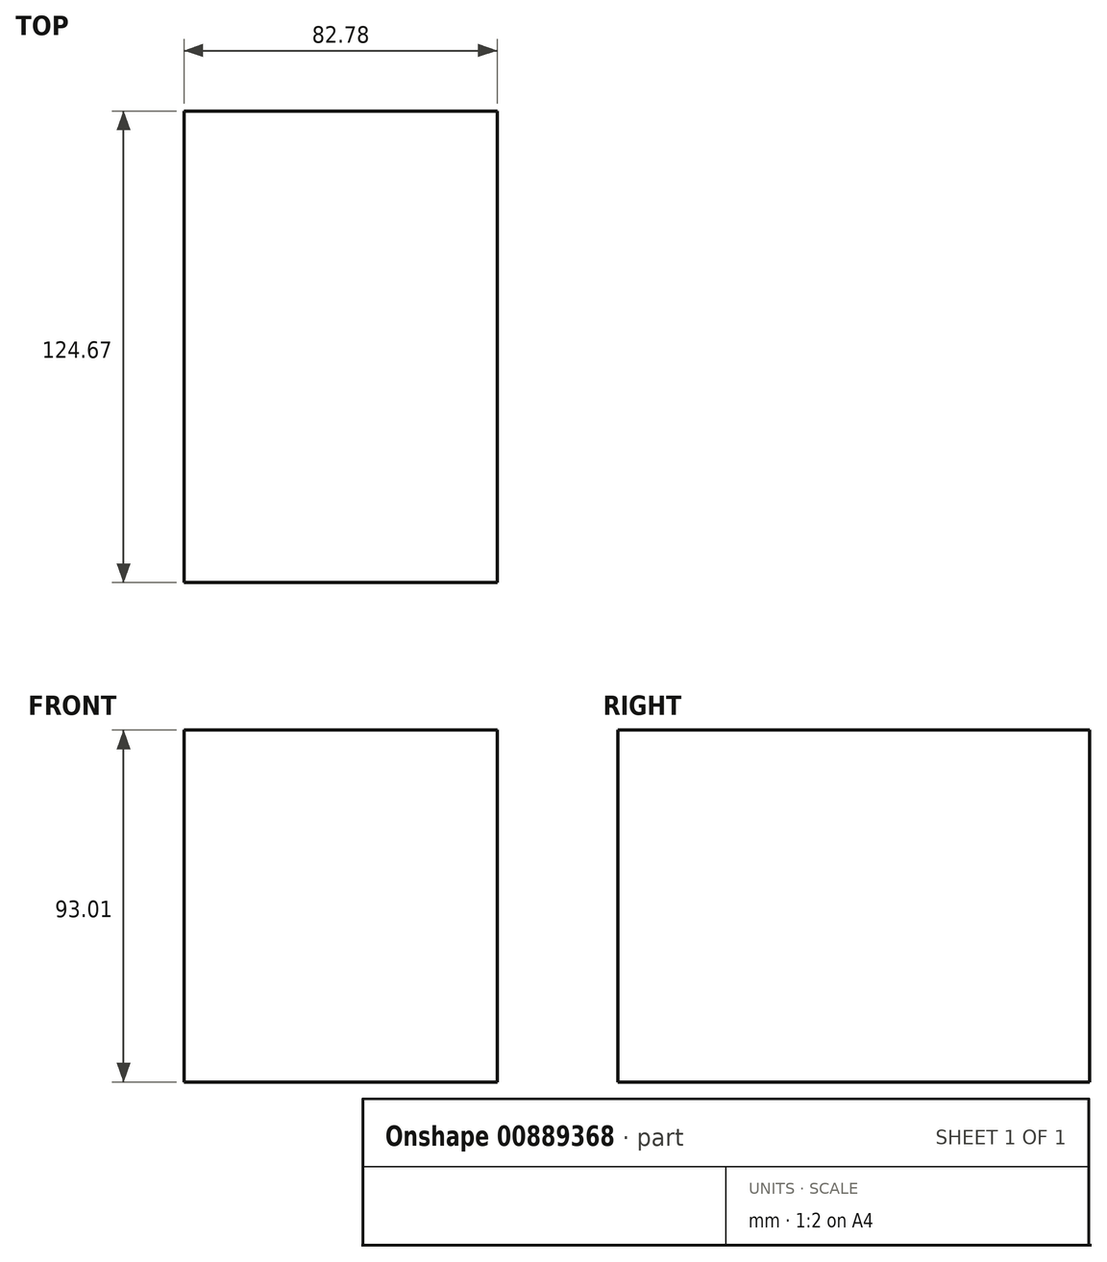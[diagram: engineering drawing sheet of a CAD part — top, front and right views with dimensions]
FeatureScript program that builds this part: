
annotation { "Feature Type Name" : "Feature", "Feature Type Description" : "" }
export const myFeature = defineFeature(function(context is Context, id is Id, definition is map)
    precondition{}
    {
        {
            var Q0;
            Q0=qCreatedBy(makeId("Front.planeOp"),FACE);
            var sketch = newSketch(context, id + "F0", { "sketchPlane" : qUnion([Q0])});
            skLineSegment(sketch, "E0.bottom", {"start": v(-41.4, 0) * mm, "end": v(41.4, 0) * mm});
            skLineSegment(sketch, "E0.top", {"start": v(-41.4, 93) * mm, "end": v(41.4, 93) * mm});
            skLineSegment(sketch, "E0.left", {"start": v(-41.4, 0) * mm, "end": v(-41.4, 93) * mm});
            skLineSegment(sketch, "E0.right", {"start": v(41.4, 0) * mm, "end": v(41.4, 93) * mm});
            skPoint(sketch, "E0.middle", {"position": v(0, 46.5) * mm});
            skSolve(sketch);
        }
        {
            var Q0;
            Q0=makeQuery(id+"F0.imprint","IMPRINT",FACE,{"disambiguationData":[TD([[makeQuery(id+"F0.imprint","IMPRINT",EDGE,{"derivedFrom":sQuery(id+"F0.wireOp",EDGE,"E0.bottom")}),1.0]])]});
            extrude(context, id + "F1", {"entities" : qUnion([Q0]), "depth" : 124.67 * mm, "offsetDistance" : 25.4 * mm});
        }
    });
